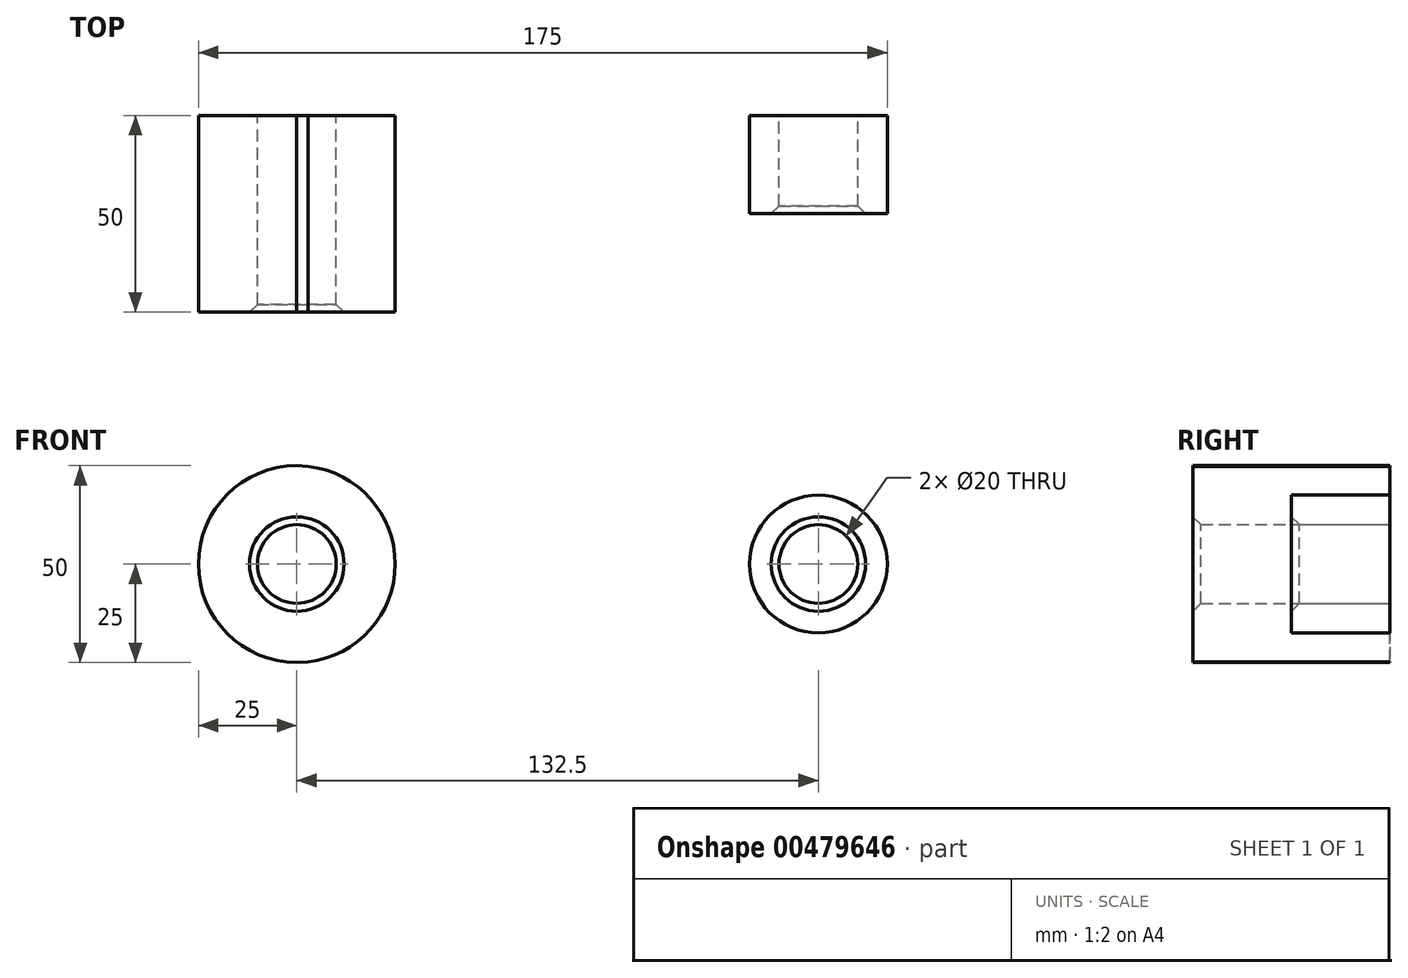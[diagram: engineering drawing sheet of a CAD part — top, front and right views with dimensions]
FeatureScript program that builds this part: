
annotation { "Feature Type Name" : "Feature", "Feature Type Description" : "" }
export const myFeature = defineFeature(function(context is Context, id is Id, definition is map)
    precondition{}
    {
        {
            var Q0;
            Q0=qCreatedBy(makeId("Front.planeOp"),FACE);
            var sketch = newSketch(context, id + "F0", { "sketchPlane" : qUnion([Q0])});
            skCircle(sketch, "E0", {"center": v(0, 0) * mm, "radius": 25 * mm});
            skCircle(sketch, "E1", {"center": v(132.5, 0) * mm, "radius": 17.5 * mm});
            skLineSegment(sketch, "E2", {"start": v(0, 25) * mm, "end": v(133.49, 17.47) * mm});
            skLineSegment(sketch, "E3", {"start": v(0, -25) * mm, "end": v(133.49, -17.47) * mm});
            skCircle(sketch, "E4", {"center": v(0, 0) * mm, "radius": 10 * mm});
            skCircle(sketch, "E5", {"center": v(132.5, 0) * mm, "radius": 10 * mm});
            skSolve(sketch);
        }
        {
            var Q0;
            {var subQ0=sQuery(id+"F0.wireOp",EDGE,"E2");var subQ1=sQuery(id+"F0.wireOp",EDGE,"E0");var subQ2=makeQuery(id+"F0.imprint","INTERSECT",VERTEX,{"disambiguationData":[OD(1.0)],"derivedFrom":[subQ1,subQ0]});Q0=makeQuery(id+"F0.imprint","IMPRINT",FACE,{"disambiguationData":[TD([[makeQuery(id+"F0.imprint","IMPRINT",EDGE,{"disambiguationData":[TD([[subQ2,1.0]])],"derivedFrom":subQ1}),-1.0]])]});}
            var Q1;
            Q1=makeQuery(id+"F0.imprint","IMPRINT",FACE,{"disambiguationData":[TD([[makeQuery(id+"F0.imprint","IMPRINT",EDGE,{"derivedFrom":sQuery(id+"F0.wireOp",EDGE,"E4")}),-1.0]])]});
            var Q2;
            Q2=makeQuery(id+"F0.imprint","IMPRINT",FACE,{"disambiguationData":[TD([[makeQuery(id+"F0.imprint","IMPRINT",EDGE,{"derivedFrom":sQuery(id+"F0.wireOp",EDGE,"E5")}),-1.0]])]});
            extrude(context, id + "F1", {"entities" : qUnion([Q0, Q1, Q2]), "depth" : 25 * mm});
        }
        {
            var Q0;
            Q0=makeQuery(id+"F0.imprint","IMPRINT",FACE,{"disambiguationData":[TD([[makeQuery(id+"F0.imprint","IMPRINT",EDGE,{"derivedFrom":sQuery(id+"F0.wireOp",EDGE,"E4")}),-1.0]])]});
            extrude(context, id + "F2", {"entities" : qUnion([Q0]), "operationType" : NewBodyOperationType.ADD, "depth" : 50 * mm});
        }
        {
            var Q0;
            Q0=makeQuery(id+"F2.opExtrude","CAP_EDGE",EDGE,{"disambiguationData":[OSD([sQuery(id+"F0.wireOp",EDGE,"E4")])],"isStart":false});
            var Q1;
            {var subQ0=sQuery(id+"F0.wireOp",EDGE,"E0");Q1=makeQuery(id+"F2.opExtrude","CAP_EDGE",EDGE,{"disambiguationData":[OSD([subQ0]),TDD([makeQuery(id+"F0.imprint","IMPRINT",EDGE,{"disambiguationData":[TD([[makeQuery(id+"F0.imprint","INTERSECT",VERTEX,{"disambiguationData":[OD(1.0)],"derivedFrom":[subQ0,sQuery(id+"F0.wireOp",EDGE,"E2")]}),1.0]])],"derivedFrom":subQ0})])],"isStart":false});}
            var Q2;
            Q2=makeQuery(id+"F1.opExtrude","CAP_EDGE",EDGE,{"disambiguationData":[OSD([sQuery(id+"F0.wireOp",EDGE,"E5")])],"isStart":false});
            chamfer(context, id + "F3", {"entities" : qUnion([Q0, Q1, Q2]), "width" : 2 * mm, "tangentPropagation" : true});
        }
    });
